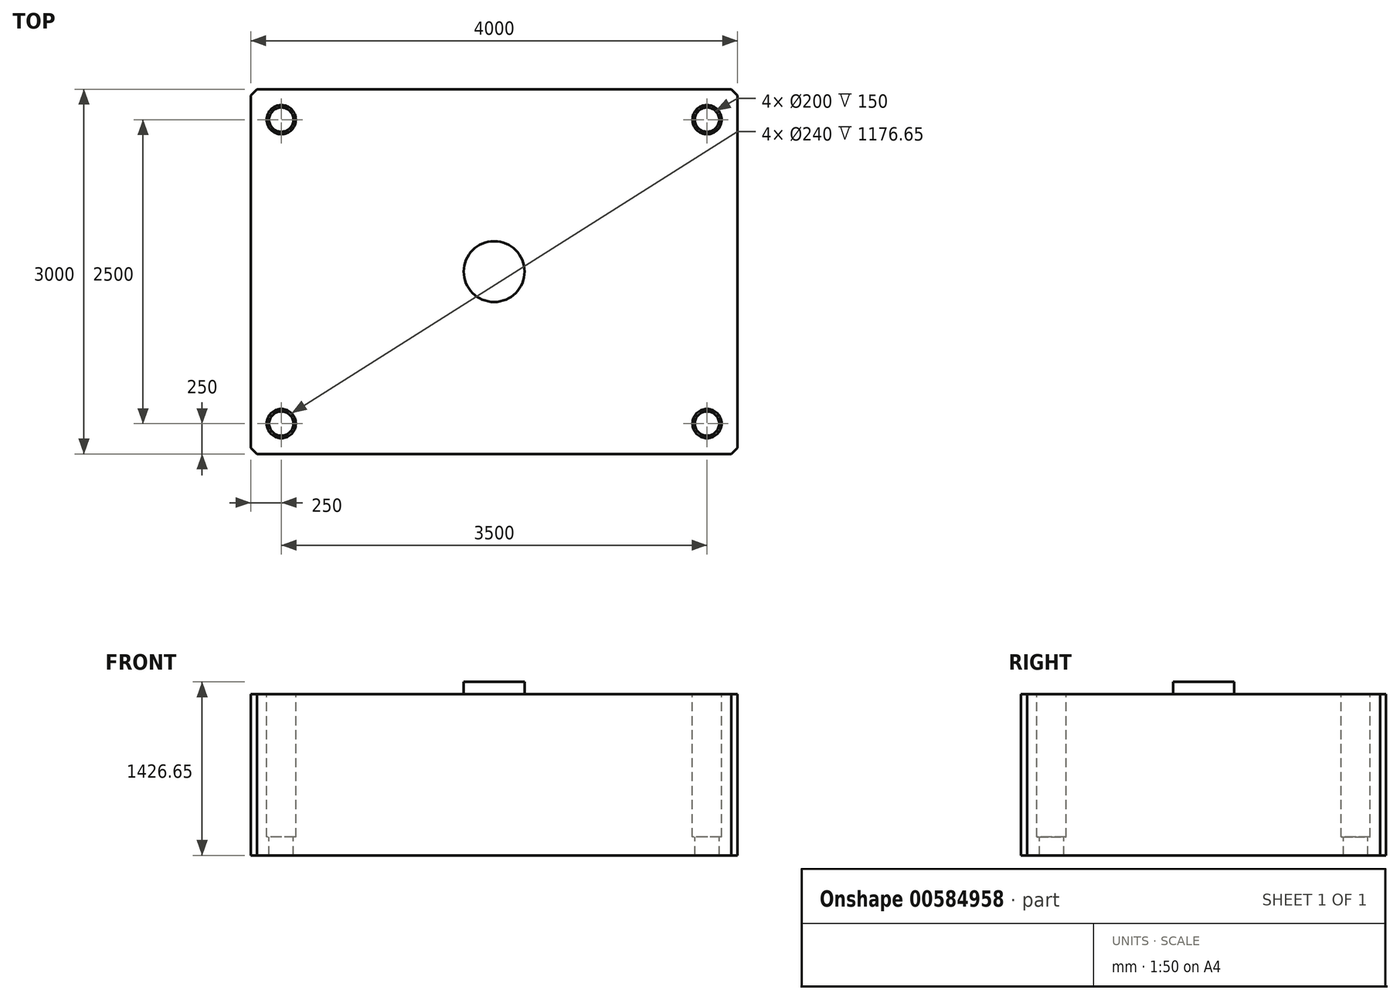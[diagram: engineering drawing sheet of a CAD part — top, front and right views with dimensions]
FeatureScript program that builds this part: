
annotation { "Feature Type Name" : "Feature", "Feature Type Description" : "" }
export const myFeature = defineFeature(function(context is Context, id is Id, definition is map)
    precondition{}
    {
        {
            var Q0;
            Q0=qCreatedBy(makeId("Top.planeOp"),FACE);
            var sketch = newSketch(context, id + "F0", { "sketchPlane" : qUnion([Q0])});
            skLineSegment(sketch, "E0.bottom", {"start": v(2000, -1500) * mm, "end": v(-2000, -1500) * mm});
            skLineSegment(sketch, "E0.top", {"start": v(2000, 1500) * mm, "end": v(-2000, 1500) * mm});
            skLineSegment(sketch, "E0.left", {"start": v(2000, -1500) * mm, "end": v(2000, 1500) * mm});
            skLineSegment(sketch, "E0.right", {"start": v(-2000, -1500) * mm, "end": v(-2000, 1500) * mm});
            skPoint(sketch, "E0.middle", {"position": v(0, 0) * mm});
            skSolve(sketch);
        }
        {
            var Q0;
            Q0=qSketchRegion(id+"F0",true);
            extrude(context, id + "F1", {"entities" : qUnion([Q0]), "oppositeDirection" : true, "depth" : 200 * mm, "offsetDistance" : 25 * mm, "symmetric" : true});
        }
        {
            var Q0;
            Q0=makeQuery(id+"F1.opExtrude","SWEPT_EDGE",EDGE,{"disambiguationData":[OSD([sQuery(id+"F0.wireOp",EDGE,"E0.bottom"),sQuery(id+"F0.wireOp",EDGE,"E0.right")])]});
            var Q1;
            Q1=makeQuery(id+"F1.opExtrude","SWEPT_EDGE",EDGE,{"disambiguationData":[OSD([sQuery(id+"F0.wireOp",EDGE,"E0.top"),sQuery(id+"F0.wireOp",EDGE,"E0.left")])]});
            var Q2;
            Q2=makeQuery(id+"F1.opExtrude","SWEPT_EDGE",EDGE,{"disambiguationData":[OSD([sQuery(id+"F0.wireOp",EDGE,"E0.bottom"),sQuery(id+"F0.wireOp",EDGE,"E0.left")])]});
            var Q3;
            Q3=makeQuery(id+"F1.opExtrude","SWEPT_EDGE",EDGE,{"disambiguationData":[OSD([sQuery(id+"F0.wireOp",EDGE,"E0.top"),sQuery(id+"F0.wireOp",EDGE,"E0.right")])]});
            chamfer(context, id + "F2", {"entities" : qUnion([Q0, Q1, Q2, Q3]), "width" : 50 * mm, "tangentPropagation" : true});
        }
        {
            var Q0;
            Q0=makeQuery(id+"F1.opExtrude","CAP_FACE",FACE,{"disambiguationData":[OSD([sQuery(id+"F0.wireOp",EDGE,"E0.bottom"),sQuery(id+"F0.wireOp",EDGE,"E0.top"),sQuery(id+"F0.wireOp",EDGE,"E0.left"),sQuery(id+"F0.wireOp",EDGE,"E0.right")])],"isStart":true});
            var sketch = newSketch(context, id + "F3", { "sketchPlane" : qUnion([Q0])});
            skLineSegment(sketch, "E1.bottom", {"start": v(-1750, 1250) * mm, "end": v(1750, 1250) * mm, "construction": true});
            skLineSegment(sketch, "E1.top", {"start": v(-1750, -1250) * mm, "end": v(1750, -1250) * mm, "construction": true});
            skLineSegment(sketch, "E1.left", {"start": v(-1750, 1250) * mm, "end": v(-1750, -1250) * mm, "construction": true});
            skLineSegment(sketch, "E1.right", {"start": v(1750, 1250) * mm, "end": v(1750, -1250) * mm, "construction": true});
            skLineSegment(sketch, "E2", {"start": v(2000, 0) * mm, "end": v(1750, 0) * mm, "construction": true});
            skLineSegment(sketch, "E3", {"start": v(1750, 0) * mm, "end": v(1750, 0) * mm});
            skLineSegment(sketch, "E4", {"start": v(0, 1500) * mm, "end": v(0, 1250) * mm, "construction": true});
            skPoint(sketch, "E5", {"position": v(0, 1250) * mm});
            skSolve(sketch);
        }
        {
            var Q0;
            Q0=sQuery(id+"F3.wireOp",VERTEX,"E1.bottom.start");
            var Q1;
            Q1=sQuery(id+"F3.wireOp",VERTEX,"E1.right.start");
            var Q2;
            Q2=sQuery(id+"F3.wireOp",VERTEX,"E1.top.start");
            var Q3;
            Q3=sQuery(id+"F3.wireOp",VERTEX,"E1.right.end");
            var Q4;
            Q4=makeQuery(id+"F1.opExtrude","SWEPT_BODY",BODY,{"disambiguationData":[OSD([sQuery(id+"F0.wireOp",EDGE,"E0.bottom"),sQuery(id+"F0.wireOp",EDGE,"E0.top"),sQuery(id+"F0.wireOp",EDGE,"E0.left"),sQuery(id+"F0.wireOp",EDGE,"E0.right")])]});
            hole(context, id + "F4", {"style" : HoleStyle.SIMPLE, "endStyle" : HoleEndStyle.THROUGH, "holeDiameter" : 200 * mm, "majorDiameter" : 5 * mm, "isTappedThrough" : true, "tappedDepth" : 12 * mm, "tapClearance" : 3, "locations" : qUnion([Q0, Q1, Q2, Q3]), "scope" : qUnion([Q4])});
        }
        {
            var Q0;
            Q0=makeQuery(id+"F1.opExtrude","CAP_FACE",FACE,{"disambiguationData":[OSD([sQuery(id+"F0.wireOp",EDGE,"E0.bottom"),sQuery(id+"F0.wireOp",EDGE,"E0.top"),sQuery(id+"F0.wireOp",EDGE,"E0.left"),sQuery(id+"F0.wireOp",EDGE,"E0.right")])],"isStart":true});
            var sketch = newSketch(context, id + "F5", { "sketchPlane" : qUnion([Q0])});
            skCircle(sketch, "E6", {"center": v(-1750, 1250) * mm, "radius": 120 * mm});
            skCircle(sketch, "E7", {"center": v(1750, 1250) * mm, "radius": 120 * mm});
            skCircle(sketch, "E8", {"center": v(-1750, -1250) * mm, "radius": 120 * mm});
            skCircle(sketch, "E9", {"center": v(1750, -1250) * mm, "radius": 120 * mm});
            skSolve(sketch);
        }
        {
            var Q0;
            Q0=makeQuery(id+"F5.imprint","IMPRINT",FACE,{"disambiguationData":[TD([[makeQuery(id+"F5.imprint","IMPRINT",EDGE,{"derivedFrom":sQuery(id+"F5.wireOp",EDGE,"E8")}),1.0]])]});
            var Q1;
            Q1=makeQuery(id+"F5.imprint","IMPRINT",FACE,{"disambiguationData":[TD([[makeQuery(id+"F5.imprint","IMPRINT",EDGE,{"derivedFrom":sQuery(id+"F5.wireOp",EDGE,"E6")}),1.0]])]});
            var Q2;
            Q2=makeQuery(id+"F5.imprint","IMPRINT",FACE,{"disambiguationData":[TD([[makeQuery(id+"F5.imprint","IMPRINT",EDGE,{"derivedFrom":sQuery(id+"F5.wireOp",EDGE,"E7")}),1.0]])]});
            var Q3;
            Q3=makeQuery(id+"F5.imprint","IMPRINT",FACE,{"disambiguationData":[TD([[makeQuery(id+"F5.imprint","IMPRINT",EDGE,{"derivedFrom":sQuery(id+"F5.wireOp",EDGE,"E9")}),1.0]])]});
            extrude(context, id + "F6", {"entities" : qUnion([Q0, Q1, Q2, Q3]), "operationType" : NewBodyOperationType.REMOVE, "oppositeDirection" : true, "depth" : 50 * mm, "offsetDistance" : 25 * mm});
        }
        {
            var Q0;
            Q0=makeQuery(id+"F1.opExtrude","CAP_FACE",FACE,{"disambiguationData":[OSD([sQuery(id+"F0.wireOp",EDGE,"E0.bottom"),sQuery(id+"F0.wireOp",EDGE,"E0.top"),sQuery(id+"F0.wireOp",EDGE,"E0.left"),sQuery(id+"F0.wireOp",EDGE,"E0.right")])],"isStart":true});
            extrude(context, id + "F7", {"entities" : qUnion([Q0]), "operationType" : NewBodyOperationType.ADD, "depth" : 1126.65 * mm, "offsetDistance" : 25 * mm});
        }
        {
            var Q0;
            Q0=makeQuery(id+"F7.opExtrude","CAP_FACE",FACE,{"disambiguationData":[OSD([sQuery(id+"F0.wireOp",EDGE,"E0.bottom"),sQuery(id+"F0.wireOp",EDGE,"E0.top"),sQuery(id+"F0.wireOp",EDGE,"E0.left"),sQuery(id+"F0.wireOp",EDGE,"E0.right")])],"isStart":false});
            var sketch = newSketch(context, id + "F8", { "sketchPlane" : qUnion([Q0])});
            skCircle(sketch, "E10", {"center": v(0, 0) * mm, "radius": 250 * mm});
            skSolve(sketch);
        }
        {
            var Q0;
            Q0=makeQuery(id+"F8.imprint","IMPRINT",FACE,{"disambiguationData":[TD([[makeQuery(id+"F8.imprint","IMPRINT",EDGE,{"derivedFrom":sQuery(id+"F8.wireOp",EDGE,"E10")}),1.0]])]});
            var sketch = newSketch(context, id + "F9", { "sketchPlane" : qUnion([Q0])});
            skSolve(sketch);
        }
        {
            var Q0;
            Q0=makeQuery(id+"F9.imprint","IMPRINT",FACE,{"disambiguationData":[TD([[makeQuery(id+"F9.imprint","IMPRINT",EDGE,{"derivedFrom":makeQuery(id+"F8.imprint","IMPRINT",EDGE,{"derivedFrom":sQuery(id+"F8.wireOp",EDGE,"E10")})}),1.0]])]});
            extrude(context, id + "F10", {"entities" : qUnion([Q0]), "depth" : 100 * mm, "offsetDistance" : 25 * mm});
        }
    });
